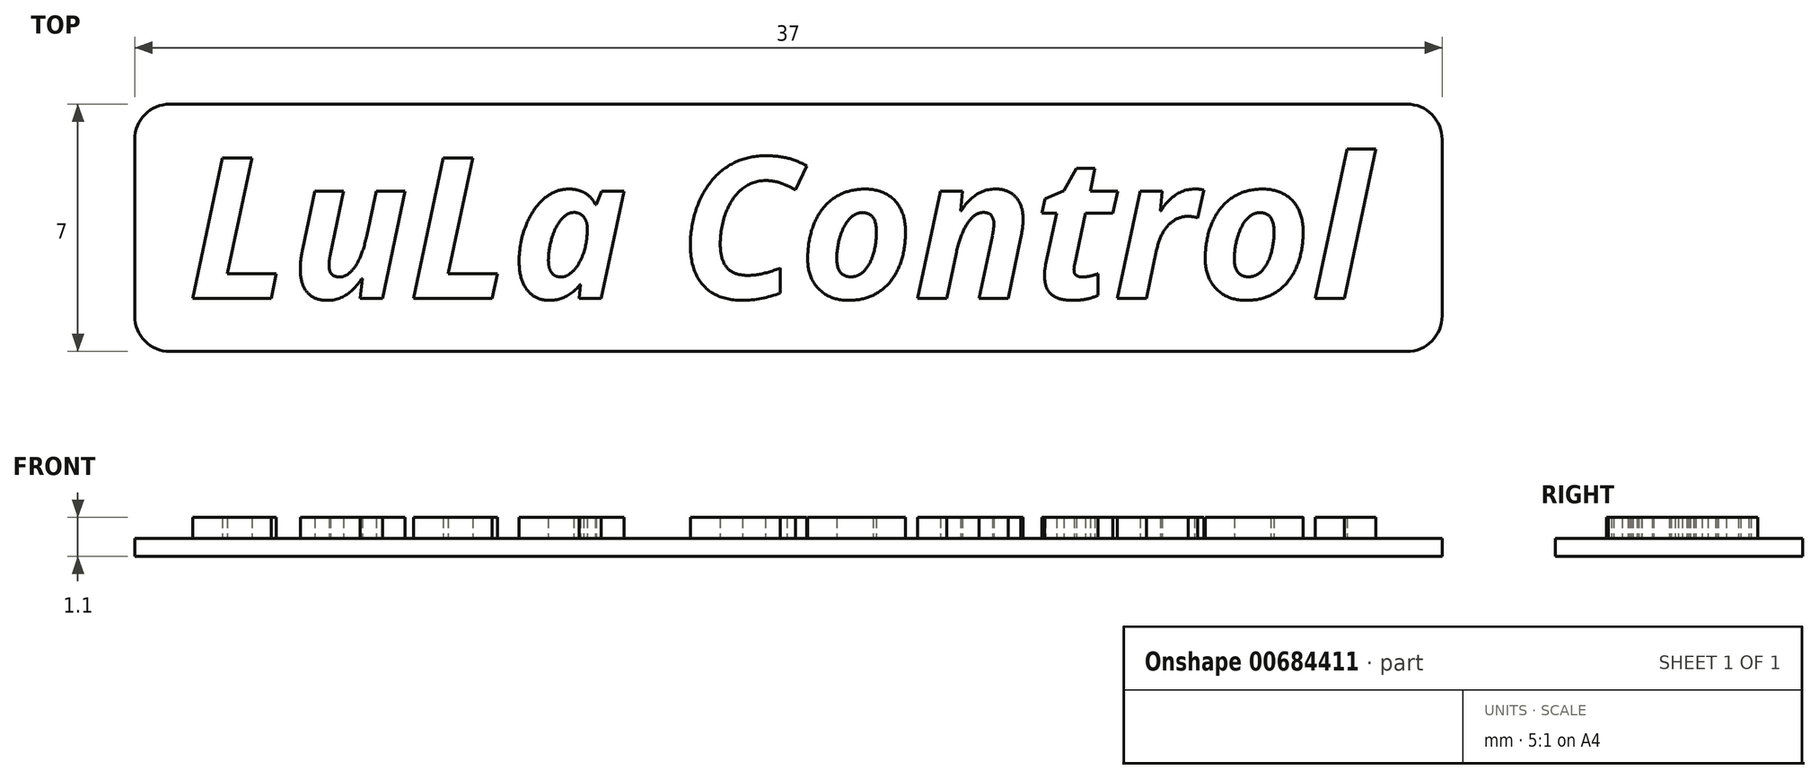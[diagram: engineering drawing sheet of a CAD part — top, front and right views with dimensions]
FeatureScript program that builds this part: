
annotation { "Feature Type Name" : "Feature", "Feature Type Description" : "" }
export const myFeature = defineFeature(function(context is Context, id is Id, definition is map)
    precondition{}
    {
        {
            var Q0;
            Q0=qCreatedBy(makeId("Top.planeOp"),FACE);
            var sketch = newSketch(context, id + "F0", { "sketchPlane" : qUnion([Q0])});
            skLineSegment(sketch, "E0.bottom", {"start": v(-17.5, 3.5) * mm, "end": v(17.5, 3.5) * mm});
            skLineSegment(sketch, "E0.top", {"start": v(-17.5, -3.5) * mm, "end": v(17.5, -3.5) * mm});
            skLineSegment(sketch, "E0.left", {"start": v(-18.5, 2.5) * mm, "end": v(-18.5, -2.5) * mm});
            skLineSegment(sketch, "E0.right", {"start": v(18.5, 2.5) * mm, "end": v(18.5, -2.5) * mm});
            skPoint(sketch, "E0.middle", {"position": v(0, 0) * mm});
            skPoint(sketch, "E1.visualSharp", {"position": v(-18.5, 3.5) * mm});
            skArc(sketch, "E1.filletArc", {"start": v(-17.5, 3.5) * mm, "mid": v(-18.2, 3.2) * mm, "end": v(-18.5, 2.5) * mm});
            skPoint(sketch, "E2.visualSharp", {"position": v(-18.5, -3.5) * mm});
            skArc(sketch, "E2.filletArc", {"start": v(-18.5, -2.5) * mm, "mid": v(-18.2, -3.2) * mm, "end": v(-17.5, -3.5) * mm});
            skPoint(sketch, "E3.visualSharp", {"position": v(18.5, -3.5) * mm});
            skArc(sketch, "E3.filletArc", {"start": v(17.5, -3.5) * mm, "mid": v(18.2, -3.2) * mm, "end": v(18.5, -2.5) * mm});
            skPoint(sketch, "E4.visualSharp", {"position": v(18.5, 3.5) * mm});
            skArc(sketch, "E4.filletArc", {"start": v(18.5, 2.5) * mm, "mid": v(18.2, 3.2) * mm, "end": v(17.5, 3.5) * mm});
            skSolve(sketch);
        }
        {
            var Q0;
            Q0=makeQuery(id+"F0.imprint","IMPRINT",FACE,{"disambiguationData":[TD([[makeQuery(id+"F0.imprint","IMPRINT",EDGE,{"derivedFrom":sQuery(id+"F0.wireOp",EDGE,"E0.bottom")}),-1.0]])]});
            extrude(context, id + "F1", {"entities" : qUnion([Q0]), "depth" : .5 * mm, "offsetDistance" : 25 * mm});
        }
        {
            var Q0;
            Q0=makeQuery(id+"F1.opExtrude","CAP_FACE",FACE,{"disambiguationData":[OSD([sQuery(id+"F0.wireOp",EDGE,"E0.bottom"),sQuery(id+"F0.wireOp",EDGE,"E0.top"),sQuery(id+"F0.wireOp",EDGE,"E0.left"),sQuery(id+"F0.wireOp",EDGE,"E0.right")])],"isStart":false});
            var sketch = newSketch(context, id + "F2", { "sketchPlane" : qUnion([Q0])});
            skText(sketch, "E5", { "text": "LuLa Control\n", "fontName": "OpenSans-BoldItalic.ttf"});
            const initialGuessF2  = {"E5": [-0.017, -0.002, 1, 0, 0.00401]};
            skSetInitialGuess(sketch, initialGuessF2);
            skSolve(sketch);
        }
        {
            var Q0;
            Q0 = qSketchRegion(id + "F2", true);
            extrude(context, id + "F3", {"entities" : qUnion([Q0]), "operationType" : NewBodyOperationType.ADD, "depth" : .6 * mm, "offsetDistance" : 25 * mm});
        }
    });
